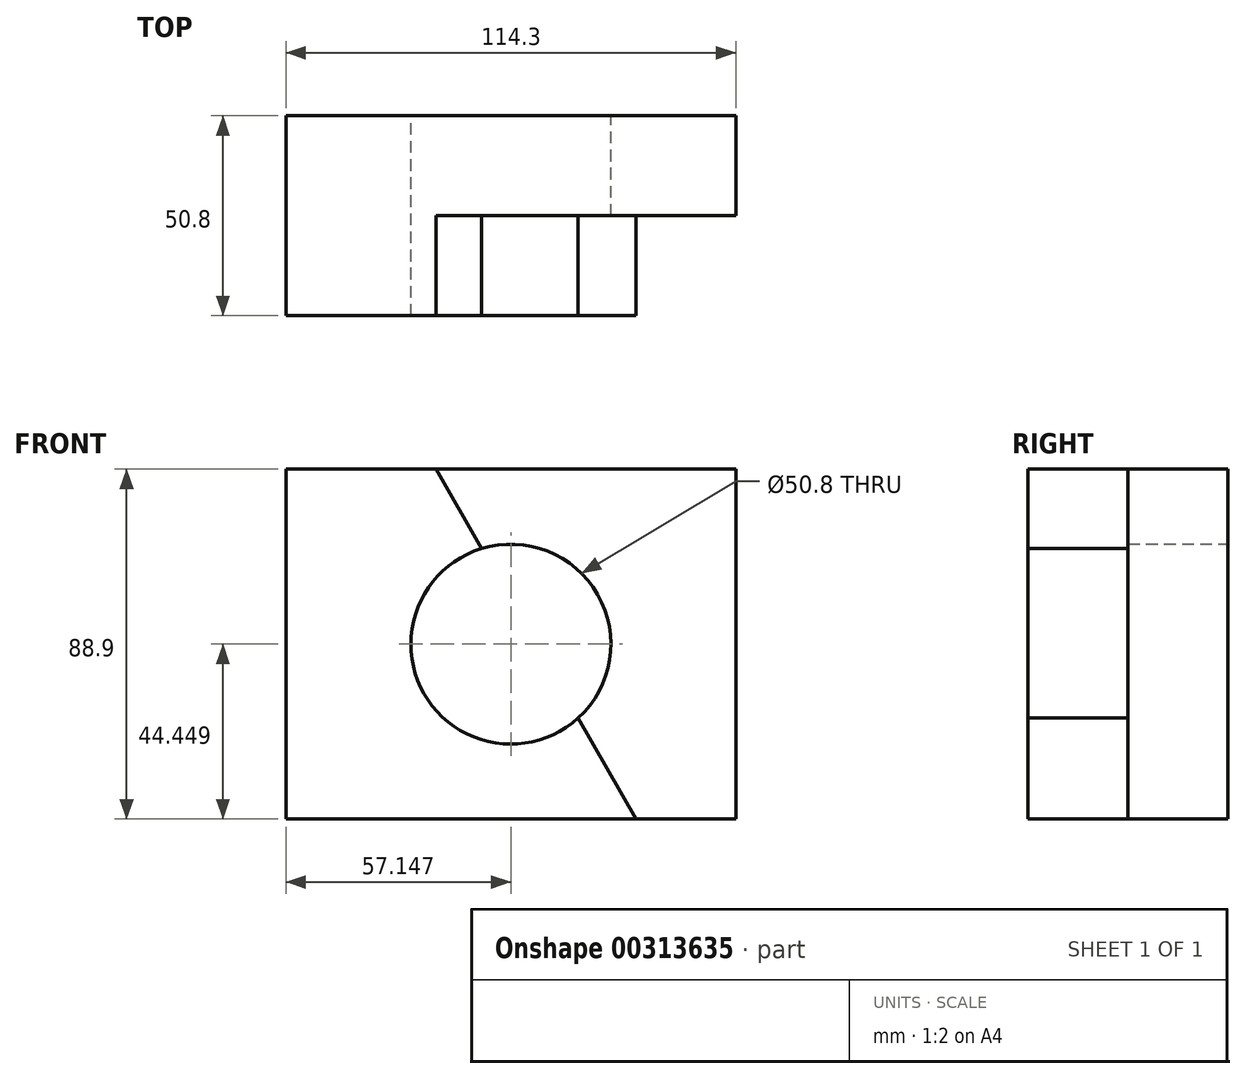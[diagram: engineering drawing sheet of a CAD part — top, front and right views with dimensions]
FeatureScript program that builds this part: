
annotation { "Feature Type Name" : "Feature", "Feature Type Description" : "" }
export const myFeature = defineFeature(function(context is Context, id is Id, definition is map)
    precondition{}
    {
        {
            var Q0;
            Q0=qCreatedBy(makeId("Front.planeOp"),FACE);
            var sketch = newSketch(context, id + "F0", { "sketchPlane" : qUnion([Q0])});
            skLineSegment(sketch, "E0.bottom", {"start": v(-58.44, 44.25) * mm, "end": v(55.86, 44.25) * mm});
            skLineSegment(sketch, "E0.top", {"start": v(-58.44, -44.65) * mm, "end": v(55.86, -44.65) * mm});
            skLineSegment(sketch, "E0.left", {"start": v(-58.44, 44.25) * mm, "end": v(-58.44, -44.65) * mm});
            skLineSegment(sketch, "E0.right", {"start": v(55.86, 44.25) * mm, "end": v(55.86, -44.65) * mm});
            skLineSegment(sketch, "E1", {"start": v(-58.44, 44.25) * mm, "end": v(-58.44, -0.2) * mm});
            skCircle(sketch, "E2", {"center": v(-1.3, -0.2) * mm, "radius": 25.4 * mm});
            skPoint(sketch, "E2.centerSnap0", {"position": v(-1.3, 44.25) * mm});
            skSolve(sketch);
        }
        {
            var Q0;
            Q0=makeQuery(id+"F0.imprint","IMPRINT",FACE,{"disambiguationData":[TD([[makeQuery(id+"F0.imprint","IMPRINT",EDGE,{"derivedFrom":sQuery(id+"F0.wireOp",EDGE,"E0.bottom")}),-1.0]])]});
            extrude(context, id + "F1", {"entities" : qUnion([Q0]), "depth" : 50.8 * mm});
        }
        {
            var Q0;
            Q0=makeQuery(id+"F1.opExtrude","CAP_FACE",FACE,{"disambiguationData":[OSD([sQuery(id+"F0.wireOp",EDGE,"E0.bottom"),sQuery(id+"F0.wireOp",EDGE,"E0.top"),sQuery(id+"F0.wireOp",EDGE,"E0.left"),sQuery(id+"F0.wireOp",EDGE,"E0.right")])],"isStart":false});
            var sketch = newSketch(context, id + "F2", { "sketchPlane" : qUnion([Q0])});
            skLineSegment(sketch, "E3", {"start": v(-20.34, 44.25) * mm, "end": v(30.46, -44.65) * mm});
            skSolve(sketch);
        }
        {
            var Q0;
            {var subQ0=sQuery(id+"F2.wireOp",EDGE,"E3");Q0=makeQuery(id+"F2.imprint","IMPRINT",FACE,{"disambiguationData":[TD([[makeQuery(id+"F2.imprint","IMPRINT",EDGE,{"derivedFrom":subQ0}),1.0]])]});}
            extrude(context, id + "F3", {"entities" : qUnion([Q0]), "operationType" : NewBodyOperationType.REMOVE, "oppositeDirection" : true, "depth" : 25.4 * mm});
        }
    });
